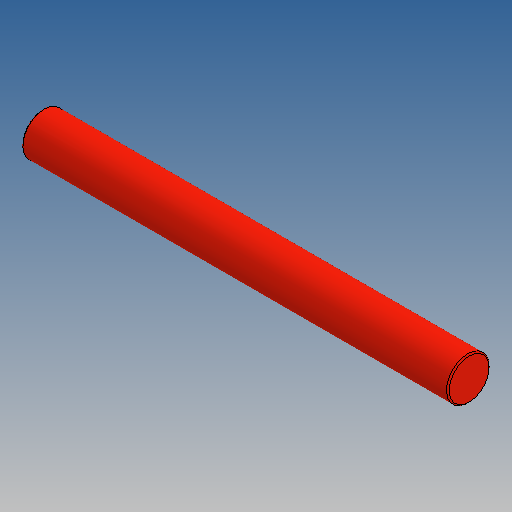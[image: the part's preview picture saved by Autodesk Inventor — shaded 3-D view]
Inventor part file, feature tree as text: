
AUTODESK INVENTOR PART (.ipt)
format: ipt  version: 2025.1 (Build 291241000, 241)  size: 121,344 bytes
history: native  units: mm (DEFAULTED — no unit token found)
features: extrude x1, fillet x1, sketch x1
ambient origin geometry x8: Origin, YZ Plane, XZ Plane, XY Plane, X Axis, Y Axis, Z Axis, Center Point
bodies: Solid2 (feature_tree)
feature tree (3):
  extrude  "Extrusion7"  Depth=32.0mm TaperAngle=0.0deg
  fillet  "Fillet2"  Radius=0.1mm
  sketch  "Sketch1"  dims[d26=3.2mm d27=32.0mm d28=0.0mm d29=0.1mm d30=0.0mm d31=0.0mm]
